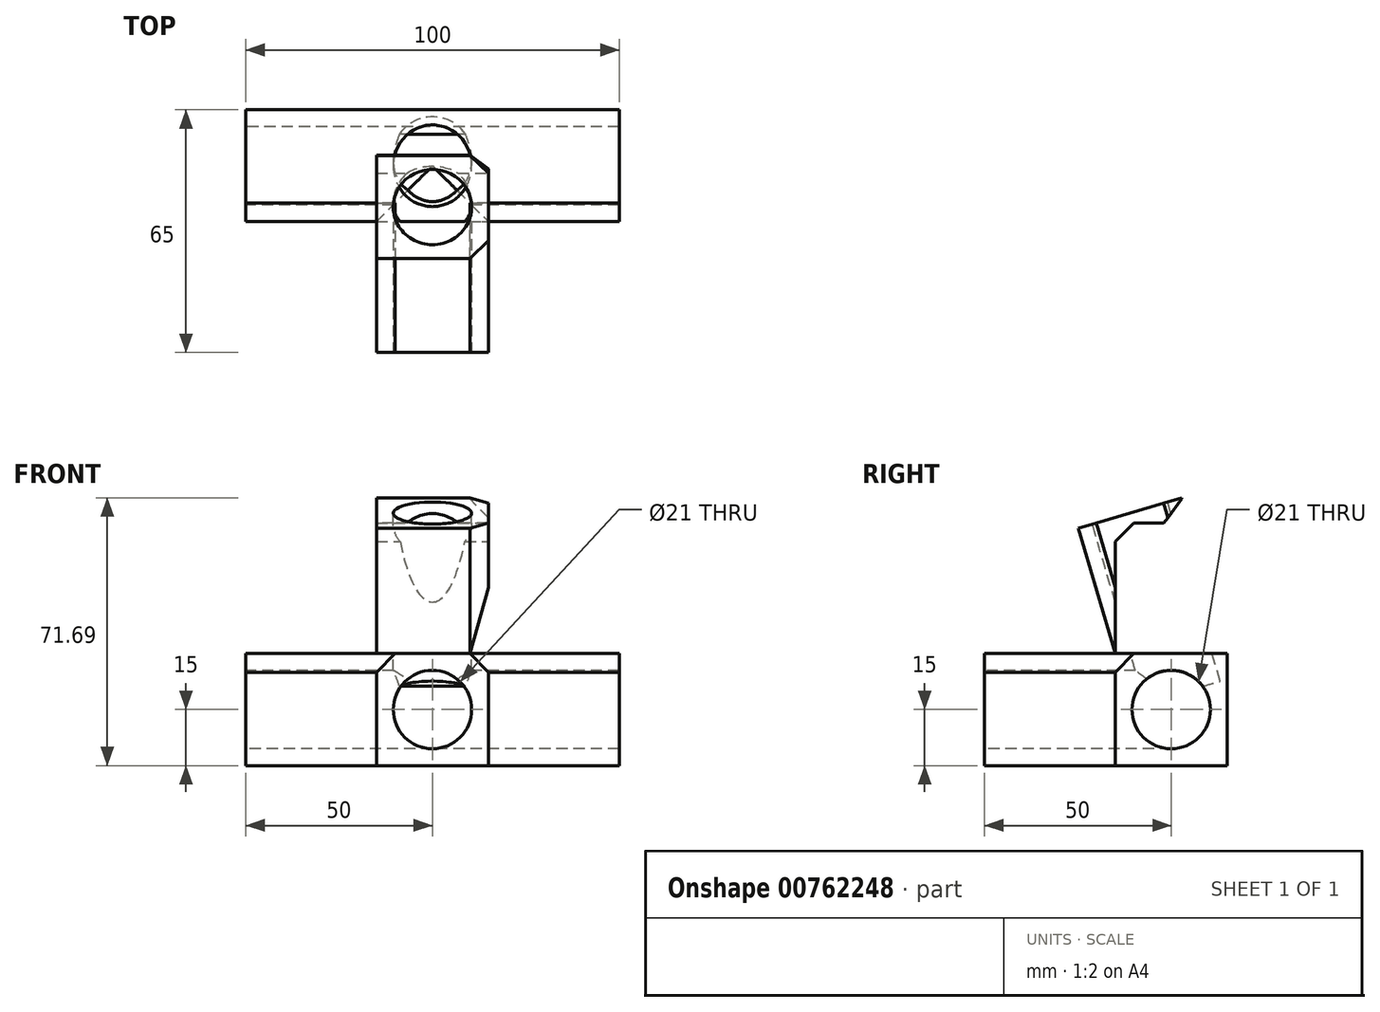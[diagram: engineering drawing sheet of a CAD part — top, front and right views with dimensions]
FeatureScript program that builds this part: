
annotation { "Feature Type Name" : "Feature", "Feature Type Description" : "" }
export const myFeature = defineFeature(function(context is Context, id is Id, definition is map)
    precondition{}
    {
        {
            var Q0;
            Q0=qCreatedBy(makeId("Top.planeOp"),FACE);
            var sketch = newSketch(context, id + "F0", { "sketchPlane" : qUnion([Q0])});
            skLineSegment(sketch, "E0.bottom", {"start": v(50, 15) * mm, "end": v(-50, 15) * mm});
            skLineSegment(sketch, "E0.top", {"start": v(50, -15) * mm, "end": v(-50, -15) * mm});
            skLineSegment(sketch, "E0.left", {"start": v(50, 15) * mm, "end": v(50, -15) * mm});
            skLineSegment(sketch, "E0.right", {"start": v(-50, 15) * mm, "end": v(-50, -15) * mm});
            skPoint(sketch, "E0.middle", {"position": v(0, 0) * mm});
            skSolve(sketch);
        }
        {
            var Q0;
            Q0=makeQuery(id+"F0.imprint","IMPRINT",FACE,{"disambiguationData":[TD([[makeQuery(id+"F0.imprint","IMPRINT",EDGE,{"derivedFrom":sQuery(id+"F0.wireOp",EDGE,"E0.bottom")}),1.0]])]});
            extrude(context, id + "F1", {"entities" : qUnion([Q0]), "depth" : 30 * mm, "offsetDistance" : 25 * mm});
        }
        {
            var Q0;
            Q0=makeQuery(id+"F1.opExtrude","CAP_FACE",FACE,{"disambiguationData":[OSD([sQuery(id+"F0.wireOp",EDGE,"E0.bottom"),sQuery(id+"F0.wireOp",EDGE,"E0.top"),sQuery(id+"F0.wireOp",EDGE,"E0.left"),sQuery(id+"F0.wireOp",EDGE,"E0.right")])],"isStart":false});
            var sketch = newSketch(context, id + "F2", { "sketchPlane" : qUnion([Q0])});
            skLineSegment(sketch, "E1.bottom", {"start": v(15, 15) * mm, "end": v(-15, 15) * mm});
            skLineSegment(sketch, "E1.top", {"start": v(15, -15) * mm, "end": v(-15, -15) * mm});
            skLineSegment(sketch, "E1.left", {"start": v(15, 15) * mm, "end": v(15, -15) * mm});
            skLineSegment(sketch, "E1.right", {"start": v(-15, 15) * mm, "end": v(-15, -15) * mm});
            skPoint(sketch, "E1.middle", {"position": v(0, 0) * mm});
            skSolve(sketch);
        }
        {
            var Q0;
            Q0=makeQuery(id+"F1.opExtrude","SWEPT_FACE",FACE,{"disambiguationData":[OSD([sQuery(id+"F0.wireOp",EDGE,"E0.right")])]});
            var sketch = newSketch(context, id + "F3", { "sketchPlane" : qUnion([Q0])});
            skCircle(sketch, "E2", {"center": v(0, 15) * mm, "radius": 10.5 * mm});
            skPoint(sketch, "E2.centerSnap0", {"position": v(15, 15) * mm});
            skPoint(sketch, "E2.centerSnap1", {"position": v(0, 30) * mm});
            skSolve(sketch);
        }
        {
            var Q0;
            Q0=makeQuery(id+"F3.imprint","IMPRINT",FACE,{"disambiguationData":[TD([[makeQuery(id+"F3.imprint","IMPRINT",EDGE,{"derivedFrom":sQuery(id+"F3.wireOp",EDGE,"E2")}),1.0]])]});
            extrude(context, id + "F4", {"entities" : qUnion([Q0]), "operationType" : NewBodyOperationType.REMOVE, "oppositeDirection" : true, "depth" : 100 * mm, "offsetDistance" : 25 * mm});
        }
        {
            var Q0;
            Q0=makeQuery(id+"F1.opExtrude","SWEPT_FACE",FACE,{"disambiguationData":[OSD([sQuery(id+"F0.wireOp",EDGE,"E0.top")])]});
            var sketch = newSketch(context, id + "F5", { "sketchPlane" : qUnion([Q0])});
            skLineSegment(sketch, "E3", {"start": v(15, 30) * mm, "end": v(15, 0) * mm});
            skLineSegment(sketch, "E4", {"start": v(-15, 30) * mm, "end": v(-15, 0) * mm});
            skSolve(sketch);
        }
        {
            var Q0;
            {var subQ0=sQuery(id+"F5.wireOp",EDGE,"E3");Q0=makeQuery(id+"F5.imprint","IMPRINT",FACE,{"disambiguationData":[TD([[makeQuery(id+"F5.imprint","IMPRINT",EDGE,{"derivedFrom":subQ0}),-1.0]])]});}
            extrude(context, id + "F6", {"entities" : qUnion([Q0]), "operationType" : NewBodyOperationType.ADD, "depth" : 35 * mm, "offsetDistance" : 25 * mm});
        }
        {
            var Q0;
            Q0=makeQuery(id+"F2.imprint","IMPRINT",FACE,{"disambiguationData":[TD([[makeQuery(id+"F2.imprint","IMPRINT",EDGE,{"derivedFrom":sQuery(id+"F2.wireOp",EDGE,"E1.bottom")}),1.0]])]});
            extrude(context, id + "F7", {"entities" : qUnion([Q0]), "operationType" : NewBodyOperationType.ADD, "depth" : 35 * mm, "offsetDistance" : 25 * mm});
        }
        {
            var Q0;
            Q0=makeQuery(id+"F7.opExtrude","SWEPT_FACE",FACE,{"disambiguationData":[OSD([sQuery(id+"F2.wireOp",EDGE,"E1.right")])]});
            var sketch = newSketch(context, id + "F8", { "sketchPlane" : qUnion([Q0])});
            skLineSegment(sketch, "E5", {"start": v(15, 30) * mm, "end": v(24.87, 63.58) * mm});
            skLineSegment(sketch, "E6", {"start": v(24.87, 63.58) * mm, "end": v(-2.75, 71.7) * mm});
            skLineSegment(sketch, "E7", {"start": v(-15, 30) * mm, "end": v(-2.75, 71.7) * mm});
            skSolve(sketch);
        }
        {
            var Q0;
            Q0=makeQuery(id+"F8.imprint","IMPRINT",FACE,{"disambiguationData":[TD([[makeQuery(id+"F8.imprint","IMPRINT",EDGE,{"derivedFrom":sQuery(id+"F8.wireOp",EDGE,"E5")}),1.0]])]});
            var Q1;
            {var subQ1=sQuery(id+"F2.wireOp",EDGE,"E1.right");var subQ2=makeQuery(id+"F7.opExtrude","CAP_EDGE",EDGE,{"disambiguationData":[OSD([subQ1])],"isStart":true});Q1=makeQuery(id+"F8.imprint","IMPRINT",FACE,{"disambiguationData":[TD([[makeQuery(id+"F8.imprint","IMPRINT",EDGE,{"derivedFrom":subQ2}),1.0]])]});}
            extrude(context, id + "F9", {"entities" : qUnion([Q0, Q1]), "operationType" : NewBodyOperationType.ADD, "depth" : 5 * mm, "offsetDistance" : 25 * mm});
        }
        {
            var Q0;
            Q0=makeQuery(id+"F7.opExtrude","CAP_FACE",FACE,{"disambiguationData":[OSD([sQuery(id+"F2.wireOp",EDGE,"E1.bottom"),sQuery(id+"F2.wireOp",EDGE,"E1.top"),sQuery(id+"F2.wireOp",EDGE,"E1.left"),sQuery(id+"F2.wireOp",EDGE,"E1.right")])],"isStart":false});
            var Q1;
            {var subQ0=sQuery(id+"F5.wireOp",EDGE,"E4");var subQ1=sQuery(id+"F5.wireOp",EDGE,"E3");var subQ2=sQuery(id+"F0.wireOp",EDGE,"E0.top");var subQ3=makeQuery(id+"F1.opExtrude","CAP_FACE",FACE,{"disambiguationData":[OSD([sQuery(id+"F0.wireOp",EDGE,"E0.bottom"),subQ2,sQuery(id+"F0.wireOp",EDGE,"E0.left"),sQuery(id+"F0.wireOp",EDGE,"E0.right")])],"isStart":false});var subQ4=makeQuery(id+"F1.opExtrude","CAP_EDGE",EDGE,{"disambiguationData":[OSD([subQ2])],"isStart":false});var subQ5=makeQuery(id+"F6.opExtrude","SWEPT_FACE",FACE,{"disambiguationData":[OSD([subQ2]),TDD([makeQuery(id+"F5.imprint","IMPRINT",EDGE,{"disambiguationData":[TD([[makeQuery(id+"F5.imprint","INTERSECT",VERTEX,{"derivedFrom":[subQ4,subQ1]}),-1.0]])],"derivedFrom":subQ4})])]});Q1=makeQuery(id+"F7.boolean.opBoolean","SPLIT",FACE,{"disambiguationData":[TD([makeQuery(id+"F6.opExtrude","CAP_FACE",FACE,{"disambiguationData":[OSD([subQ2,subQ1,subQ0])],"isStart":false})])],"derivedFrom":makeQuery(id+"F6.boolean.opBoolean","MERGE",FACE,{"derivedFrom":[subQ3,subQ5]})});}
            extrude(context, id + "F10", {"entities" : qUnion([Q0]), "operationType" : NewBodyOperationType.REMOVE, "endBound" : BoundingType.UP_TO_SURFACE, "oppositeDirection" : true, "depth" : 25 * mm, "endBoundEntityFace" : qUnion([Q1]), "offsetDistance" : 25 * mm});
        }
        {
            var Q0;
            {var subQ1=sQuery(id+"F2.wireOp",EDGE,"E1.right");var subQ2=makeQuery(id+"F7.opExtrude","CAP_EDGE",EDGE,{"disambiguationData":[OSD([subQ1])],"isStart":true});Q0=makeQuery(id+"F8.imprint","IMPRINT",FACE,{"disambiguationData":[TD([[makeQuery(id+"F8.imprint","IMPRINT",EDGE,{"derivedFrom":subQ2}),1.0]])]});}
            var Q1;
            Q1=makeQuery(id+"F8.imprint","IMPRINT",FACE,{"disambiguationData":[TD([[makeQuery(id+"F8.imprint","IMPRINT",EDGE,{"derivedFrom":sQuery(id+"F8.wireOp",EDGE,"E5")}),1.0]])]});
            extrude(context, id + "F11", {"entities" : qUnion([Q0, Q1]), "operationType" : NewBodyOperationType.ADD, "oppositeDirection" : true, "depth" : 30 * mm, "offsetDistance" : 25 * mm});
        }
        {
            var Q0;
            Q0=makeQuery(id+"F9.opExtrude","CAP_FACE",FACE,{"disambiguationData":[OSD([sQuery(id+"F2.wireOp",EDGE,"E1.right"),sQuery(id+"F8.wireOp",EDGE,"E5"),sQuery(id+"F8.wireOp",EDGE,"E6"),sQuery(id+"F8.wireOp",EDGE,"E7")])],"isStart":false});
            extrude(context, id + "F12", {"entities" : qUnion([Q0]), "operationType" : NewBodyOperationType.REMOVE, "oppositeDirection" : true, "depth" : 5 * mm, "offsetDistance" : 25 * mm});
        }
        {
            var Q0;
            Q0=makeQuery(id+"F6.opExtrude","CAP_FACE",FACE,{"disambiguationData":[OSD([sQuery(id+"F0.wireOp",EDGE,"E0.top"),sQuery(id+"F5.wireOp",EDGE,"E3"),sQuery(id+"F5.wireOp",EDGE,"E4")])],"isStart":false});
            var sketch = newSketch(context, id + "F13", { "sketchPlane" : qUnion([Q0])});
            skCircle(sketch, "E8", {"center": v(0, 15) * mm, "radius": 10.5 * mm});
            skPoint(sketch, "E8.centerSnap0", {"position": v(-15, 15) * mm});
            skPoint(sketch, "E8.centerSnap1", {"position": v(0, 30) * mm});
            skSolve(sketch);
        }
        {
            var Q0;
            Q0=makeQuery(id+"F13.imprint","IMPRINT",FACE,{"disambiguationData":[TD([[makeQuery(id+"F13.imprint","IMPRINT",EDGE,{"derivedFrom":sQuery(id+"F13.wireOp",EDGE,"E8")}),1.0]])]});
            extrude(context, id + "F14", {"entities" : qUnion([Q0]), "operationType" : NewBodyOperationType.REMOVE, "oppositeDirection" : true, "depth" : (35 + 15) * mm, "offsetDistance" : 25 * mm});
        }
        {
            var Q0;
            {var subQ0=sQuery(id+"F8.wireOp",EDGE,"E6");Q0=makeQuery(id+"F11.boolean.opBoolean","MERGE",FACE,{"derivedFrom":[makeQuery(id+"F9.opExtrude","SWEPT_FACE",FACE,{"disambiguationData":[OSD([subQ0])]}),makeQuery(id+"F11.opExtrude","SWEPT_FACE",FACE,{"disambiguationData":[OSD([subQ0])]})]});}
            var sketch = newSketch(context, id + "F15", { "sketchPlane" : qUnion([Q0])});
            skCircle(sketch, "E9", {"center": v(0, 8.46) * mm, "radius": 10.5 * mm});
            skPoint(sketch, "E9.centerSnap0", {"position": v(15, 8.46) * mm});
            skPoint(sketch, "E9.centerSnap1", {"position": v(0, -5.93) * mm});
            skSolve(sketch);
        }
        {
            var Q0;
            Q0=makeQuery(id+"F15.imprint","IMPRINT",FACE,{"disambiguationData":[TD([[makeQuery(id+"F15.imprint","IMPRINT",EDGE,{"derivedFrom":sQuery(id+"F15.wireOp",EDGE,"E9")}),1.0]])]});
            extrude(context, id + "F16", {"entities" : qUnion([Q0]), "operationType" : NewBodyOperationType.REMOVE, "oppositeDirection" : true, "depth" : (35 + 15) * mm, "offsetDistance" : 25 * mm});
        }
        {
            var Q0;
            Q0=makeQuery(id+"F12.boolean.opBoolean","COPY",EDGE,{"derivedFrom":makeQuery(id+"F12.opExtrude","CAP_EDGE",EDGE,{"disambiguationData":[OSD([sQuery(id+"F8.wireOp",EDGE,"E7")])],"isStart":false})});
            var Q1;
            Q1=makeQuery(id+"F11.opExtrude","CAP_EDGE",EDGE,{"disambiguationData":[OSD([sQuery(id+"F8.wireOp",EDGE,"E7")])],"isStart":false});
            var Q2;
            Q2=makeQuery(id+"F11.opExtrude","CAP_EDGE",EDGE,{"disambiguationData":[OSD([sQuery(id+"F8.wireOp",EDGE,"E5")])],"isStart":false});
            var Q3;
            Q3=makeQuery(id+"F12.boolean.opBoolean","COPY",EDGE,{"derivedFrom":makeQuery(id+"F12.opExtrude","CAP_EDGE",EDGE,{"disambiguationData":[OSD([sQuery(id+"F8.wireOp",EDGE,"E5")])],"isStart":false})});
            chamfer(context, id + "F17", {"entities" : qUnion([Q0, Q1, Q2, Q3]), "width" : 5 * mm, "tangentPropagation" : true});
        }
        {
            var Q0;
            {var subQ0=sQuery(id+"F8.wireOp",EDGE,"E7");var subQ1=sQuery(id+"F2.wireOp",EDGE,"E1.right");var subQ2=sQuery(id+"F2.wireOp",EDGE,"E1.bottom");var subQ3=sQuery(id+"F0.wireOp",EDGE,"E0.bottom");var subQ7=sQuery(id+"F0.wireOp",EDGE,"E0.left");var subQ8=sQuery(id+"F0.wireOp",EDGE,"E0.right");var subQ12=makeQuery(id+"F1.opExtrude","CAP_EDGE",EDGE,{"disambiguationData":[OSD([subQ3])],"isStart":false});var subQ13=makeQuery(id+"F7.boolean.opBoolean","SPLIT",EDGE,{"disambiguationData":[TD([makeQuery(id+"F1.opExtrude","SWEPT_FACE",FACE,{"disambiguationData":[OSD([subQ8])]})])],"derivedFrom":subQ12});var subQ14=makeQuery(id+"F11.boolean.opBoolean","MERGE",EDGE,{"derivedFrom":[makeQuery(id+"F9.boolean.opBoolean","MERGE",EDGE,{"derivedFrom":[subQ13,makeQuery(id+"F9.opExtrude","SWEPT_EDGE",EDGE,{"disambiguationData":[OSD([subQ3,subQ2,subQ1,subQ0])]})]}),makeQuery(id+"F10.boolean.opBoolean","MERGE",EDGE,{"derivedFrom":[makeQuery(id+"F7.boolean.opBoolean","SPLIT",EDGE,{"disambiguationData":[TD([makeQuery(id+"F1.opExtrude","SWEPT_FACE",FACE,{"disambiguationData":[OSD([subQ7])]})])],"derivedFrom":subQ12}),makeQuery(id+"F10.opExtrude","CAP_EDGE",EDGE,{"disambiguationData":[OSD([subQ2])],"isStart":false})]}),makeQuery(id+"F11.opExtrude","SWEPT_EDGE",EDGE,{"disambiguationData":[OSD([subQ3,subQ2,subQ1,subQ0])]})]});Q0=makeQuery(id+"F17.opChamfer","MERGE",EDGE,{"derivedFrom":[makeQuery(id+"F12.boolean.opBoolean","MERGE",EDGE,{"derivedFrom":[makeQuery(id+"F9.boolean.opBoolean","SPLIT",EDGE,{"derivedFrom":subQ13}),subQ14,makeQuery(id+"F12.opExtrude","SWEPT_EDGE",EDGE,{"disambiguationData":[OSD([subQ3,subQ2,subQ1,subQ0])]})]}),makeQuery(id+"F12.boolean.opBoolean","SPLIT",EDGE,{"derivedFrom":subQ14})]});}
            var Q1;
            {var subQ0=sQuery(id+"F8.wireOp",EDGE,"E7");var subQ1=sQuery(id+"F2.wireOp",EDGE,"E1.right");var subQ2=sQuery(id+"F2.wireOp",EDGE,"E1.bottom");var subQ3=sQuery(id+"F0.wireOp",EDGE,"E0.bottom");var subQ7=sQuery(id+"F0.wireOp",EDGE,"E0.left");var subQ8=sQuery(id+"F0.wireOp",EDGE,"E0.right");var subQ12=makeQuery(id+"F1.opExtrude","CAP_EDGE",EDGE,{"disambiguationData":[OSD([subQ3])],"isStart":false});var subQ13=makeQuery(id+"F10.boolean.opBoolean","MERGE",EDGE,{"derivedFrom":[makeQuery(id+"F7.boolean.opBoolean","SPLIT",EDGE,{"disambiguationData":[TD([makeQuery(id+"F1.opExtrude","SWEPT_FACE",FACE,{"disambiguationData":[OSD([subQ7])]})])],"derivedFrom":subQ12}),makeQuery(id+"F10.opExtrude","CAP_EDGE",EDGE,{"disambiguationData":[OSD([subQ2])],"isStart":false})]});Q1=makeQuery(id+"F17.opChamfer","MERGE",EDGE,{"derivedFrom":[makeQuery(id+"F11.boolean.opBoolean","SPLIT",EDGE,{"derivedFrom":subQ13}),makeQuery(id+"F12.boolean.opBoolean","SPLIT",EDGE,{"derivedFrom":makeQuery(id+"F11.boolean.opBoolean","MERGE",EDGE,{"derivedFrom":[makeQuery(id+"F9.boolean.opBoolean","MERGE",EDGE,{"derivedFrom":[makeQuery(id+"F7.boolean.opBoolean","SPLIT",EDGE,{"disambiguationData":[TD([makeQuery(id+"F1.opExtrude","SWEPT_FACE",FACE,{"disambiguationData":[OSD([subQ8])]})])],"derivedFrom":subQ12}),makeQuery(id+"F9.opExtrude","SWEPT_EDGE",EDGE,{"disambiguationData":[OSD([subQ3,subQ2,subQ1,subQ0])]})]}),subQ13,makeQuery(id+"F11.opExtrude","SWEPT_EDGE",EDGE,{"disambiguationData":[OSD([subQ3,subQ2,subQ1,subQ0])]})]})})]});}
            var Q2;
            {var subQ0=sQuery(id+"F8.wireOp",EDGE,"E5");var subQ1=sQuery(id+"F2.wireOp",EDGE,"E1.right");var subQ2=sQuery(id+"F2.wireOp",EDGE,"E1.top");var subQ3=sQuery(id+"F0.wireOp",EDGE,"E0.top");var subQ4=sQuery(id+"F0.wireOp",EDGE,"E0.right");var subQ6=makeQuery(id+"F1.opExtrude","CAP_EDGE",EDGE,{"disambiguationData":[OSD([subQ3])],"isStart":false});var subQ7=makeQuery(id+"F6.boolean.opBoolean","SPLIT",EDGE,{"disambiguationData":[TD([makeQuery(id+"F1.opExtrude","SWEPT_FACE",FACE,{"disambiguationData":[OSD([subQ4])]})])],"derivedFrom":subQ6});Q2=makeQuery(id+"F12.boolean.opBoolean","MERGE",EDGE,{"derivedFrom":[makeQuery(id+"F9.boolean.opBoolean","MERGE",EDGE,{"derivedFrom":[subQ7,makeQuery(id+"F9.opExtrude","SWEPT_EDGE",EDGE,{"disambiguationData":[OSD([subQ3,subQ2,subQ1,subQ0])]})]}),makeQuery(id+"F9.boolean.opBoolean","SPLIT",EDGE,{"derivedFrom":subQ7}),makeQuery(id+"F12.opExtrude","SWEPT_EDGE",EDGE,{"disambiguationData":[OSD([subQ3,subQ2,subQ1,subQ0])]})]});}
            var Q3;
            {var subQ1=sQuery(id+"F0.wireOp",EDGE,"E0.top");var subQ2=sQuery(id+"F0.wireOp",EDGE,"E0.left");var subQ3=makeQuery(id+"F1.opExtrude","CAP_EDGE",EDGE,{"disambiguationData":[OSD([subQ1])],"isStart":false});Q3=makeQuery(id+"F6.boolean.opBoolean","SPLIT",EDGE,{"disambiguationData":[TD([makeQuery(id+"F1.opExtrude","SWEPT_FACE",FACE,{"disambiguationData":[OSD([subQ2])]})])],"derivedFrom":subQ3});}
            var Q4;
            {var subQ0=sQuery(id+"F5.wireOp",EDGE,"E4");var subQ1=sQuery(id+"F0.wireOp",EDGE,"E0.top");Q4=makeQuery(id+"F6.opExtrude","SWEPT_EDGE",EDGE,{"disambiguationData":[OSD([subQ1,subQ0]),TDD([makeQuery(id+"F5.imprint","INTERSECT",VERTEX,{"derivedFrom":[makeQuery(id+"F1.opExtrude","CAP_EDGE",EDGE,{"disambiguationData":[OSD([subQ1])],"isStart":false}),subQ0]})])]});}
            var Q5;
            {var subQ0=sQuery(id+"F5.wireOp",EDGE,"E3");var subQ1=sQuery(id+"F0.wireOp",EDGE,"E0.top");Q5=makeQuery(id+"F6.opExtrude","SWEPT_EDGE",EDGE,{"disambiguationData":[OSD([subQ1,subQ0]),TDD([makeQuery(id+"F5.imprint","INTERSECT",VERTEX,{"derivedFrom":[makeQuery(id+"F1.opExtrude","CAP_EDGE",EDGE,{"disambiguationData":[OSD([subQ1])],"isStart":false}),subQ0]})])]});}
            chamfer(context, id + "F18", {"entities" : qUnion([Q0, Q1, Q2, Q3, Q4, Q5]), "width" : 5 * mm, "tangentPropagation" : true});
        }
    });
